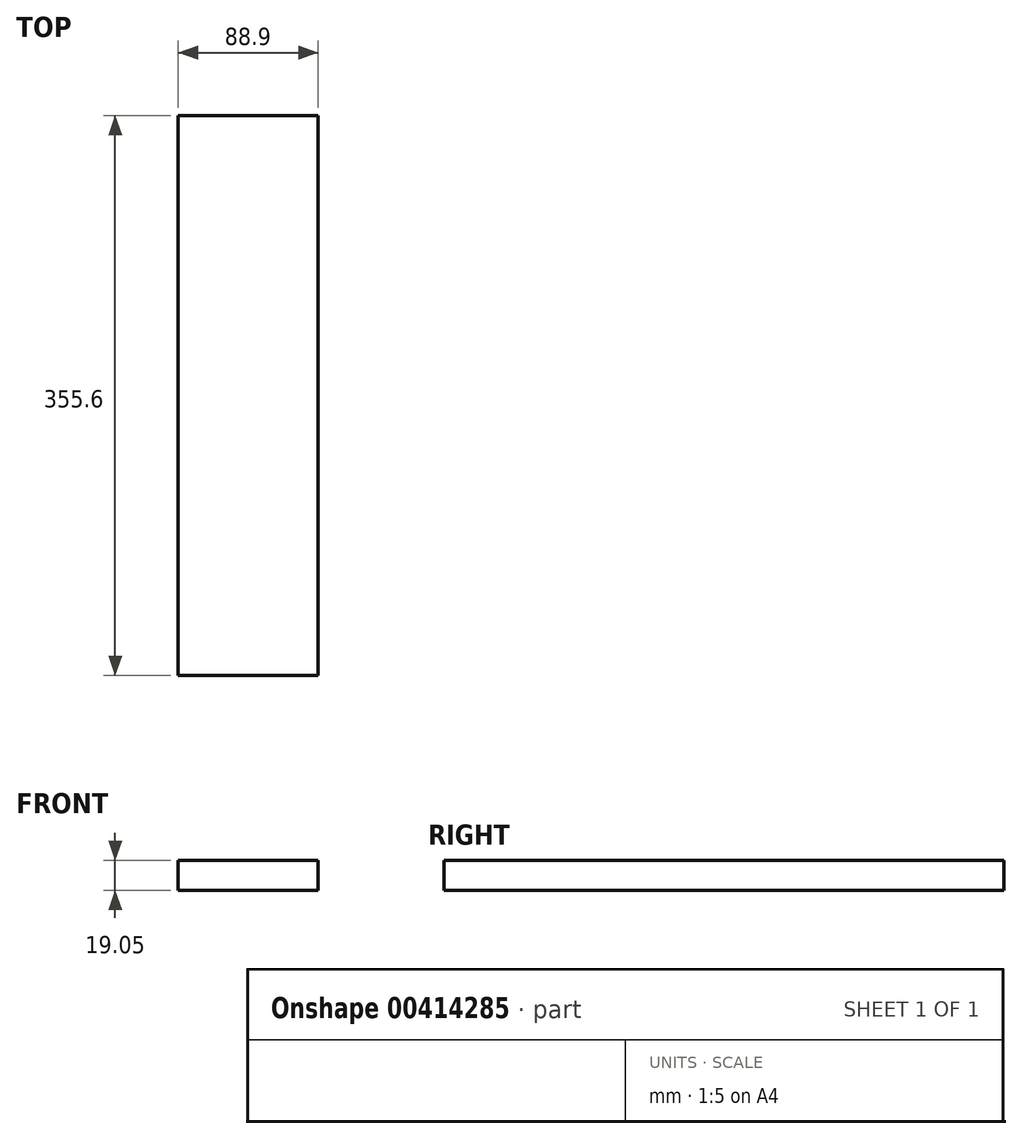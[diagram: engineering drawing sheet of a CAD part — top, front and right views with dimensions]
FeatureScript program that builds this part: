
annotation { "Feature Type Name" : "Feature", "Feature Type Description" : "" }
export const myFeature = defineFeature(function(context is Context, id is Id, definition is map)
    precondition{}
    {
        {
            var Q0;
            Q0=qCreatedBy(makeId("Front.planeOp"),FACE);
            var sketch = newSketch(context, id + "F0", { "sketchPlane" : qUnion([Q0])});
            skLineSegment(sketch, "E0.bottom", {"start": v(0, 0) * mm, "end": v(-88.9, 0) * mm});
            skLineSegment(sketch, "E0.top", {"start": v(0, 19.05) * mm, "end": v(-88.9, 19.05) * mm});
            skLineSegment(sketch, "E0.left", {"start": v(0, 0) * mm, "end": v(0, 19.05) * mm});
            skLineSegment(sketch, "E0.right", {"start": v(-88.9, 0) * mm, "end": v(-88.9, 19.05) * mm});
            skSolve(sketch);
        }
        {
            var Q0;
            Q0=qSketchRegion(id+"F0",true);
            extrude(context, id + "F1", {"entities" : qUnion([Q0]), "depth" : 355.6 * mm});
        }
    });
